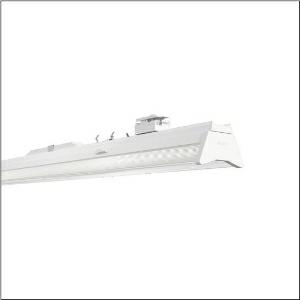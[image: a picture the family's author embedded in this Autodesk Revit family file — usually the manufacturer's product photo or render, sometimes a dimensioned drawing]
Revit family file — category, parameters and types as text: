
# Revit family: licross_21_performance_mo_52td16cn445g
name_source: partatom
category: Lighting Fixtures
units: mm (PartAtom-declared; Revit-internal decimal feet)

## family parameters
Cut with Voids When Loaded = No
Host = Face
Light Source = No
Part Type = Normal
Room Calculation Point = No
Round Connector Dimension = Use Diameter
Shared = No

## types (1)
- --- (1 x LED, 4500 lm, 24.1 W, 4000K)
    Apparent Load = 24 VA
    CIE Flux Codes = 66 88 96 79 100
    Color Rendering = 80
    Color Temperature = 4000K
    Default Elevation = 1800 mm
    Description = Licross 21 Performance MO, luminaire insert, of sheet steel, galvanised, coil coated, white, length: 1.500mm, width: 120mm, height: 123mm, LED rated luminous flux: 4.500lm, light colour: 840, SDCM (Standard Deviation of Colour Matching)MacAdam ≤ 3 SDCM (initial), control gear: ON/OFF Multilumen, CLOi, with plug, 3-pole, with phase selection, mains connection: 220..240V, AC, 50/60Hz, start of lifetime: 24W, end of service life: 28W, internal wiring halogen-free, primary light control with lens, of plastic, primary optical cover: cover, of PMMA, CAT 2 (L<= 3000cd/m²), light emission: direct/indirect distribution, primary light characteristic: symmetric, protection rating (complete): IP54, insulation class (complete): insulation class I (protective earthing), certification: CE, ENEC, UKCA, protection symbol: D if used in an environment with non-conductive dust loads with corresponding accessories, impact resistance: IK06, permissible ambient temperature for indoor applications: -35..+55°C, corresponds to IFS (International Featured Standards) requirements for safety and quality in the food industry, reducing of maximum allowable ambient temperature of 5°C with ceiling mounting, LABS conformity tested according to VDMA 24364:2018-05, The light source and the operating device comply with the requirements of the Ecodesign Regulation (EU) 2019/2020 and are replaceable in accordance with this regulation, packaging unit: 1 piece
    Height = 114 mm
    Lamp = 1 x LED
    Lamp Light Flux = 4500 lm
    Lamp Power = 24.1 W
    Lamp count = 1
    Length = 1500 mm
    Luminous efficacy = 187 lm/W
    Manufacturer = Siteco
    ModVariant = No
    Model = 52TD16CN445G
    Mounting Place = Ceiling
    Mounting Type = Pendant
    Number of Poles = 1
    OnlyDefault = Yes
    Power Factor = 1
    Product Name = Licross 21 Performance MO
    Product group = luminaire insert | ceiling pendant
    ProductGroupID = 901
    Protection Class = Protection class I
    Protection Degree = IP 54
    RLX_Detail_Level = 1
    RLX_Emergency_Light_Flux = 0 lm
    RLX_Emergency_Type = 0
    RLX_Emergency_Type_DB = No
    RlxData = <blob elided: 31669 chars, md5=7f5f395c>
    Socket = socket
    Standby Power = 0 W
    System Light Flux = 4500 lm
    System Power = 24 W
    Type Comments = factory setting: luminous flux: 100 % | (A | C | E) | 55 mA
    Type Image = l_1256138.jpg
    URL = http://relux.com
    VarID = @adj_056297
    Voltage = 0 V
    Weight = 0.00 kg
    Width = 120 mm

## geometry (parser evidence)
native form markers: Blend x4, Sweep x10
no freeform markers — native parametric forms only
